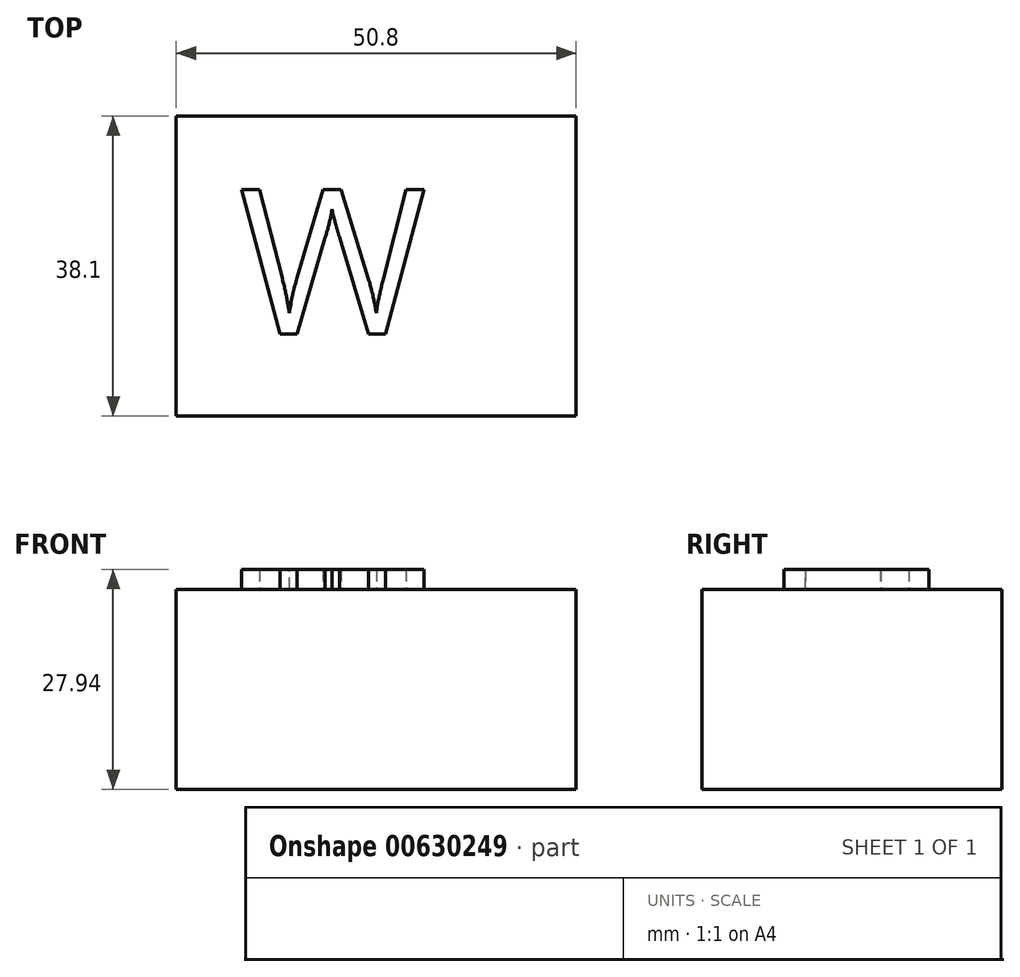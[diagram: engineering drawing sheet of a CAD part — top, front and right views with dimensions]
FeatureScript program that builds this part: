
annotation { "Feature Type Name" : "Feature", "Feature Type Description" : "" }
export const myFeature = defineFeature(function(context is Context, id is Id, definition is map)
    precondition{}
    {
        {
            var Q0;
            Q0=qCreatedBy(makeId("Top.planeOp"),FACE);
            var sketch = newSketch(context, id + "F0", { "sketchPlane" : qUnion([Q0])});
            skLineSegment(sketch, "E0.bottom", {"start": v(-50.8, 38.1) * mm, "end": v(0, 38.1) * mm});
            skLineSegment(sketch, "E0.top", {"start": v(-50.8, 0) * mm, "end": v(0, 0) * mm});
            skLineSegment(sketch, "E0.left", {"start": v(-50.8, 38.1) * mm, "end": v(-50.8, 0) * mm});
            skLineSegment(sketch, "E0.right", {"start": v(0, 38.1) * mm, "end": v(0, 0) * mm});
            skSolve(sketch);
        }
        {
            var Q0;
            Q0 = qSketchRegion(id + "F0", true);
            extrude(context, id + "F1", {"entities" : qUnion([Q0]), "depth" : 25.4 * mm, "offsetDistance" : 25.4 * mm});
        }
        {
            var Q0;
            Q0=makeQuery(id+"F1.opExtrude","CAP_FACE",FACE,{"disambiguationData":[OSD([sQuery(id+"F0.wireOp",EDGE,"E0.bottom"),sQuery(id+"F0.wireOp",EDGE,"E0.top"),sQuery(id+"F0.wireOp",EDGE,"E0.left"),sQuery(id+"F0.wireOp",EDGE,"E0.right")])],"isStart":false});
            var sketch = newSketch(context, id + "F2", { "sketchPlane" : qUnion([Q0])});
            skText(sketch, "E1", { "text": "W", "fontName": "OpenSans-Regular.ttf"});
            const initialGuessF2  = {"E1": [-0.04282, 0.0104, 1, 0, 0.01855]};
            skSetInitialGuess(sketch, initialGuessF2);
            skSolve(sketch);
        }
        {
            var Q0;
            Q0 = qSketchRegion(id + "F2", true);
            extrude(context, id + "F3", {"entities" : qUnion([Q0]), "operationType" : NewBodyOperationType.ADD, "depth" : 2.54 * mm, "offsetDistance" : 25.4 * mm});
        }
    });
